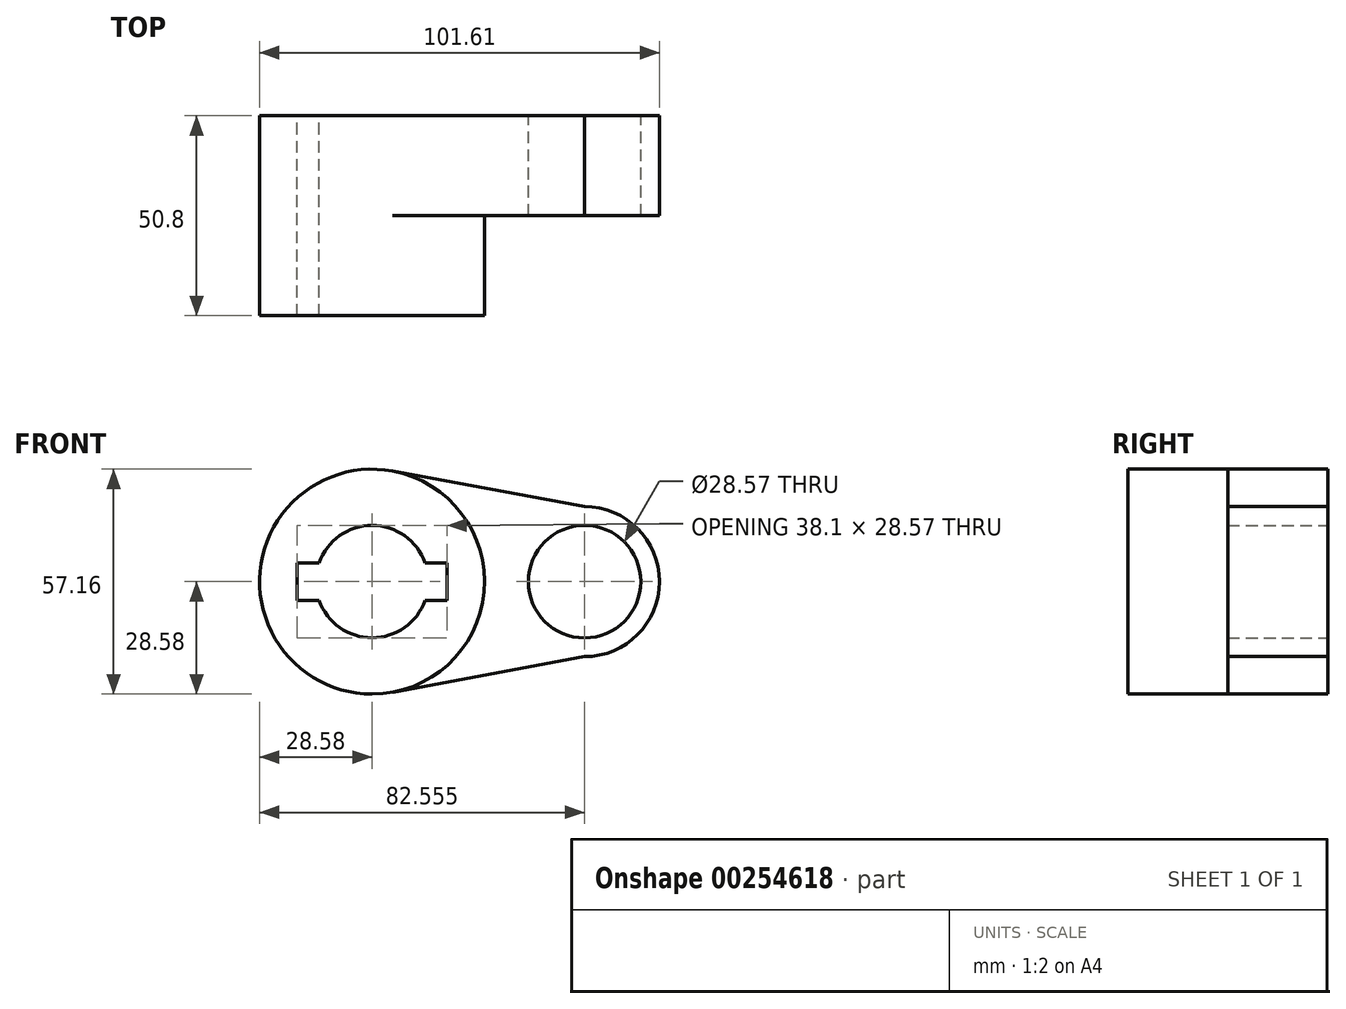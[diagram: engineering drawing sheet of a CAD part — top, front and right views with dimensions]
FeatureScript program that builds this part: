
annotation { "Feature Type Name" : "Feature", "Feature Type Description" : "" }
export const myFeature = defineFeature(function(context is Context, id is Id, definition is map)
    precondition{}
    {
        {
            var Q0;
            Q0=qCreatedBy(makeId("Front.planeOp"),FACE);
            var sketch = newSketch(context, id + "F0", { "sketchPlane" : qUnion([Q0])});
            skCircle(sketch, "E0", {"center": v(0, 0) * mm, "radius": 28.58 * mm});
            skCircle(sketch, "E1", {"center": v(53.98, 0) * mm, "radius": 19.05 * mm});
            skLineSegment(sketch, "E2", {"start": v(5.21, 28.1) * mm, "end": v(53.98, 19.05) * mm});
            skLineSegment(sketch, "E3", {"start": v(5.21, -28.1) * mm, "end": v(53.98, -19.05) * mm});
            skCircle(sketch, "E4", {"center": v(0, 0) * mm, "radius": 14.29 * mm});
            skCircle(sketch, "E5", {"center": v(53.98, 0) * mm, "radius": 14.29 * mm});
            skLineSegment(sketch, "E6.bottom", {"start": v(-19.05, 4.76) * mm, "end": v(19.05, 4.76) * mm});
            skLineSegment(sketch, "E6.top", {"start": v(-19.05, -4.76) * mm, "end": v(19.05, -4.76) * mm});
            skLineSegment(sketch, "E6.left", {"start": v(-19.05, 4.76) * mm, "end": v(-19.05, -4.76) * mm});
            skLineSegment(sketch, "E6.right", {"start": v(19.05, 4.76) * mm, "end": v(19.05, -4.76) * mm});
            skSolve(sketch);
        }
        {
            var Q0;
            {var subQ0=sQuery(id+"F0.wireOp",EDGE,"E2");Q0=makeQuery(id+"F0.imprint","IMPRINT",FACE,{"disambiguationData":[TD([[makeQuery(id+"F0.imprint","IMPRINT",EDGE,{"derivedFrom":subQ0}),-1.0]])]});}
            var Q1;
            {var subQ11=sQuery(id+"F0.wireOp",EDGE,"E6.left");Q1=makeQuery(id+"F0.imprint","IMPRINT",FACE,{"disambiguationData":[TD([[makeQuery(id+"F0.imprint","IMPRINT",EDGE,{"derivedFrom":subQ11}),-1.0]])]});}
            var Q2;
            Q2=makeQuery(id+"F0.imprint","IMPRINT",FACE,{"disambiguationData":[TD([[makeQuery(id+"F0.imprint","IMPRINT",EDGE,{"derivedFrom":sQuery(id+"F0.wireOp",EDGE,"E5")}),-1.0]])]});
            extrude(context, id + "F1", {"entities" : qUnion([Q0, Q1, Q2]), "depth" : 25.4 * mm});
        }
        {
            var Q0;
            {var subQ11=sQuery(id+"F0.wireOp",EDGE,"E6.left");Q0=makeQuery(id+"F0.imprint","IMPRINT",FACE,{"disambiguationData":[TD([[makeQuery(id+"F0.imprint","IMPRINT",EDGE,{"derivedFrom":subQ11}),-1.0]])]});}
            extrude(context, id + "F2", {"entities" : qUnion([Q0]), "operationType" : NewBodyOperationType.ADD, "depth" : 50.8 * mm});
        }
    });
